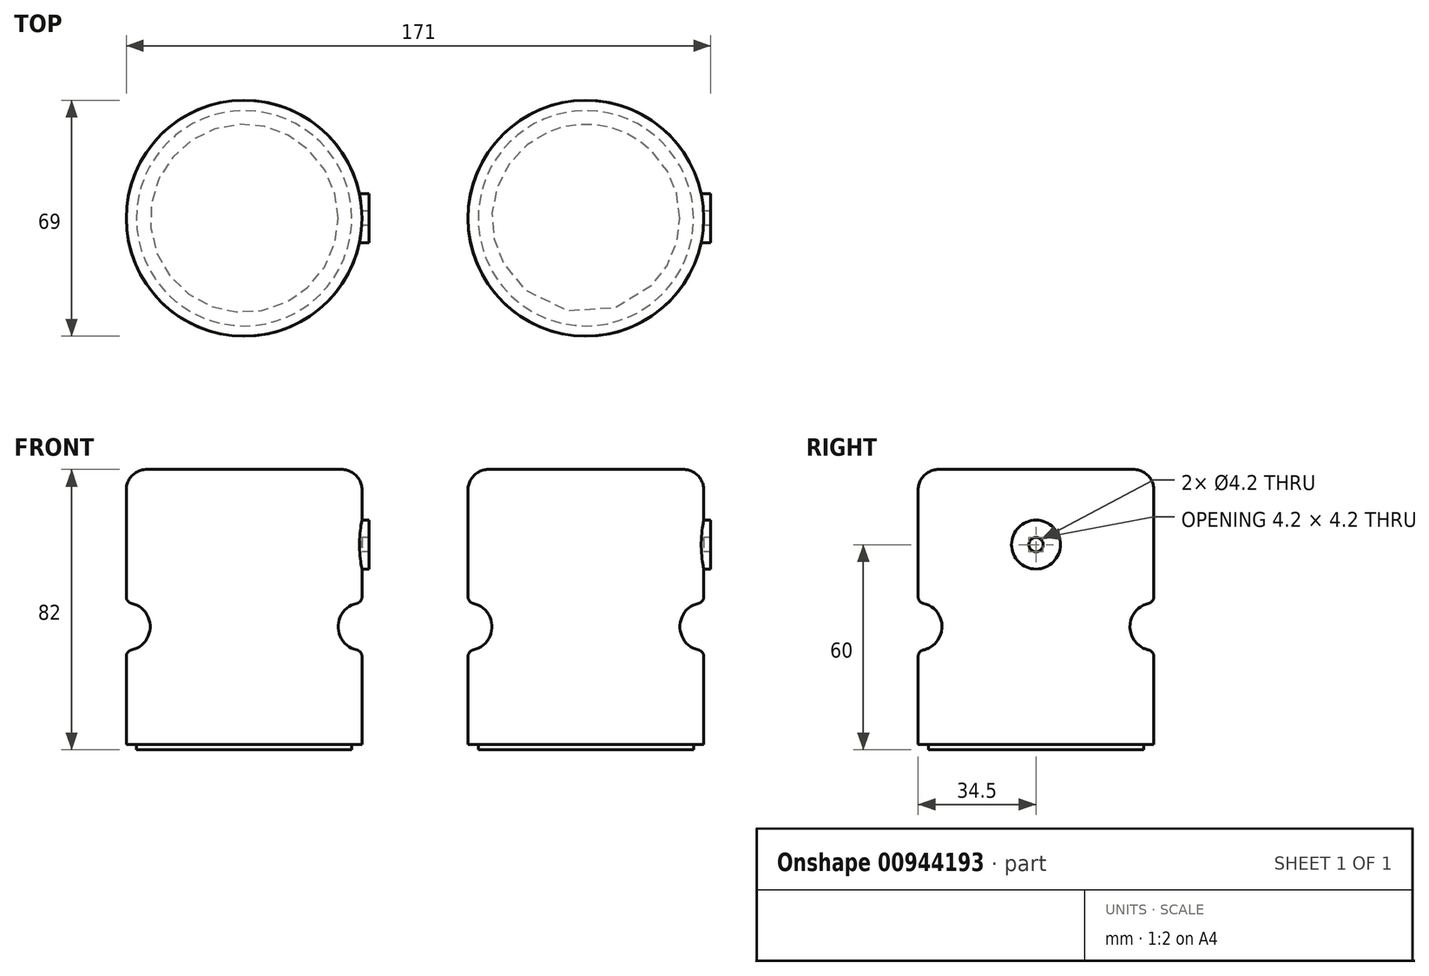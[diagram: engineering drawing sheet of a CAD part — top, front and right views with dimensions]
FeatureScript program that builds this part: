
annotation { "Feature Type Name" : "Feature", "Feature Type Description" : "" }
export const myFeature = defineFeature(function(context is Context, id is Id, definition is map)
    precondition{}
    {
        {
            var Q0;
            Q0=qCreatedBy(makeId("Front.planeOp"),FACE);
            var sketch = newSketch(context, id + "F0", { "sketchPlane" : qUnion([Q0])});
            skLineSegment(sketch, "E0", {"start": v(0, 0) * mm, "end": v(-34.5, 0) * mm});
            skLineSegment(sketch, "E1", {"start": v(-34.5, 0) * mm, "end": v(-34.5, 27.5) * mm});
            skLineSegment(sketch, "E2", {"start": v(-34.5, 27.5) * mm, "end": v(-27.5, 27.5) * mm});
            skLineSegment(sketch, "E3", {"start": v(-27.5, 27.5) * mm, "end": v(-27.5, 41.5) * mm});
            skLineSegment(sketch, "E4", {"start": v(-27.5, 41.5) * mm, "end": v(-34.5, 41.5) * mm});
            skLineSegment(sketch, "E5", {"start": v(-34.5, 41.5) * mm, "end": v(-34.5, 80.5) * mm});
            skLineSegment(sketch, "E6", {"start": v(-34.5, 80.5) * mm, "end": v(0, 80.5) * mm});
            skLineSegment(sketch, "E7", {"start": v(0, -29) * mm, "end": v(0, 108.6) * mm, "construction": true});
            skLineSegment(sketch, "E8", {"start": v(0, 80.5) * mm, "end": v(0, 0) * mm});
            skLineSegment(sketch, "E9", {"start": v(-31.5, 0) * mm, "end": v(-31.5, -1.5) * mm});
            skLineSegment(sketch, "E10", {"start": v(-31.5, -1.5) * mm, "end": v(0, -1.5) * mm});
            skLineSegment(sketch, "E11", {"start": v(0, -1.5) * mm, "end": v(0, 0) * mm});
            skSolve(sketch);
        }
        {
            var Q0;
            Q0 = qSketchRegion(id + "F0", true);
            var Q1;
            Q1=sQuery(id+"F0.wireOp",EDGE,"E7");
            revolve(context, id + "F1", {"surfaceOperationType" : NewSurfaceOperationType.NEW, "entities" : qUnion([Q0]), "axis" : qUnion([Q1]), "revolveType" : RevolveType.FULL});
        }
        {
            var Q0;
            Q0=makeQuery(id+"F1.opRevolve","SWEPT_EDGE",EDGE,{"disambiguationData":[OSD([sQuery(id+"F0.wireOp",EDGE,"E5"),sQuery(id+"F0.wireOp",EDGE,"E6")])]});
            fillet(context, id + "F2", {"entities" : qUnion([Q0]), "radius" : 6 * mm, "tangentPropagation" : true, "allowEdgeOverflow" : false});
        }
        {
            var Q0;
            Q0=makeQuery(id+"F1.opRevolve","SWEPT_EDGE",EDGE,{"disambiguationData":[OSD([sQuery(id+"F0.wireOp",EDGE,"E2"),sQuery(id+"F0.wireOp",EDGE,"E3")])]});
            var Q1;
            Q1=makeQuery(id+"F1.opRevolve","SWEPT_EDGE",EDGE,{"disambiguationData":[OSD([sQuery(id+"F0.wireOp",EDGE,"E3"),sQuery(id+"F0.wireOp",EDGE,"E4")])]});
            fillet(context, id + "F3", {"entities" : qUnion([Q0, Q1]), "radius" : 7 * mm, "tangentPropagation" : true, "allowEdgeOverflow" : false});
        }
        {
            var Q0;
            Q0=makeQuery(id+"F3.opFillet","BLEND_EDGE",EDGE,{"blendedFrom":[makeQuery(id+"F1.opRevolve","SWEPT_EDGE",EDGE,{"disambiguationData":[OSD([sQuery(id+"F0.wireOp",EDGE,"E3"),sQuery(id+"F0.wireOp",EDGE,"E4")])]}),makeQuery(id+"F1.opRevolve","SWEPT_FACE",FACE,{"disambiguationData":[OSD([sQuery(id+"F0.wireOp",EDGE,"E5")])]})],"blendedInto":[makeQuery(id+"F1.opRevolve","SWEPT_FACE",FACE,{"disambiguationData":[OSD([sQuery(id+"F0.wireOp",EDGE,"E5")])]})]});
            var Q1;
            Q1=makeQuery(id+"F3.opFillet","BLEND_EDGE",EDGE,{"blendedFrom":[makeQuery(id+"F1.opRevolve","SWEPT_EDGE",EDGE,{"disambiguationData":[OSD([sQuery(id+"F0.wireOp",EDGE,"E2"),sQuery(id+"F0.wireOp",EDGE,"E3")])]}),makeQuery(id+"F1.opRevolve","SWEPT_FACE",FACE,{"disambiguationData":[OSD([sQuery(id+"F0.wireOp",EDGE,"E1")])]})],"blendedInto":[makeQuery(id+"F1.opRevolve","SWEPT_FACE",FACE,{"disambiguationData":[OSD([sQuery(id+"F0.wireOp",EDGE,"E1")])]})]});
            fillet(context, id + "F4", {"entities" : qUnion([Q0, Q1]), "radius" : 2 * mm, "tangentPropagation" : true, "allowEdgeOverflow" : false});
        }
        {
            var Q0;
            Q0=qCreatedBy(makeId("Right.planeOp"),FACE);
            var sketch = newSketch(context, id + "F5", { "sketchPlane" : qUnion([Q0])});
            skLineSegment(sketch, "E12", {"start": v(0, -9.62) * mm, "end": v(0, 69.1) * mm, "construction": true});
            skCircle(sketch, "E13", {"center": v(0, 58.5) * mm, "radius": 7.15 * mm});
            skCircle(sketch, "E14", {"center": v(0, 58.5) * mm, "radius": 2.1 * mm});
            skSolve(sketch);
        }
        {
            var Q0;
            Q0 = qSketchRegion(id + "F5", true);
            extrude(context, id + "F6", {"entities" : qUnion([Q0]), "operationType" : NewBodyOperationType.ADD, "depth" : 36.5 * mm, "offsetDistance" : 25 * mm});
        }
        {
            var Q0;
            Q0=makeQuery(id+"F1.opRevolve","SWEPT_BODY",BODY,{"disambiguationData":[OSD([sQuery(id+"F0.wireOp",EDGE,"E0"),sQuery(id+"F0.wireOp",EDGE,"E1"),sQuery(id+"F0.wireOp",EDGE,"E2"),sQuery(id+"F0.wireOp",EDGE,"E3"),sQuery(id+"F0.wireOp",EDGE,"E4"),sQuery(id+"F0.wireOp",EDGE,"E5"),sQuery(id+"F0.wireOp",EDGE,"E6"),sQuery(id+"F0.wireOp",EDGE,"E8"),sQuery(id+"F0.wireOp",EDGE,"E9"),sQuery(id+"F0.wireOp",EDGE,"E10"),sQuery(id+"F0.wireOp",EDGE,"E11")])]});
            transform(context, id + "F7", {"entities" : qUnion([Q0]), "transformType" : TransformType.TRANSLATION_3D, "dx" : 100 * mm, "dy" : 0 * mm, "dz" : 0 * mm, "makeCopy" : true});
        }
    });
